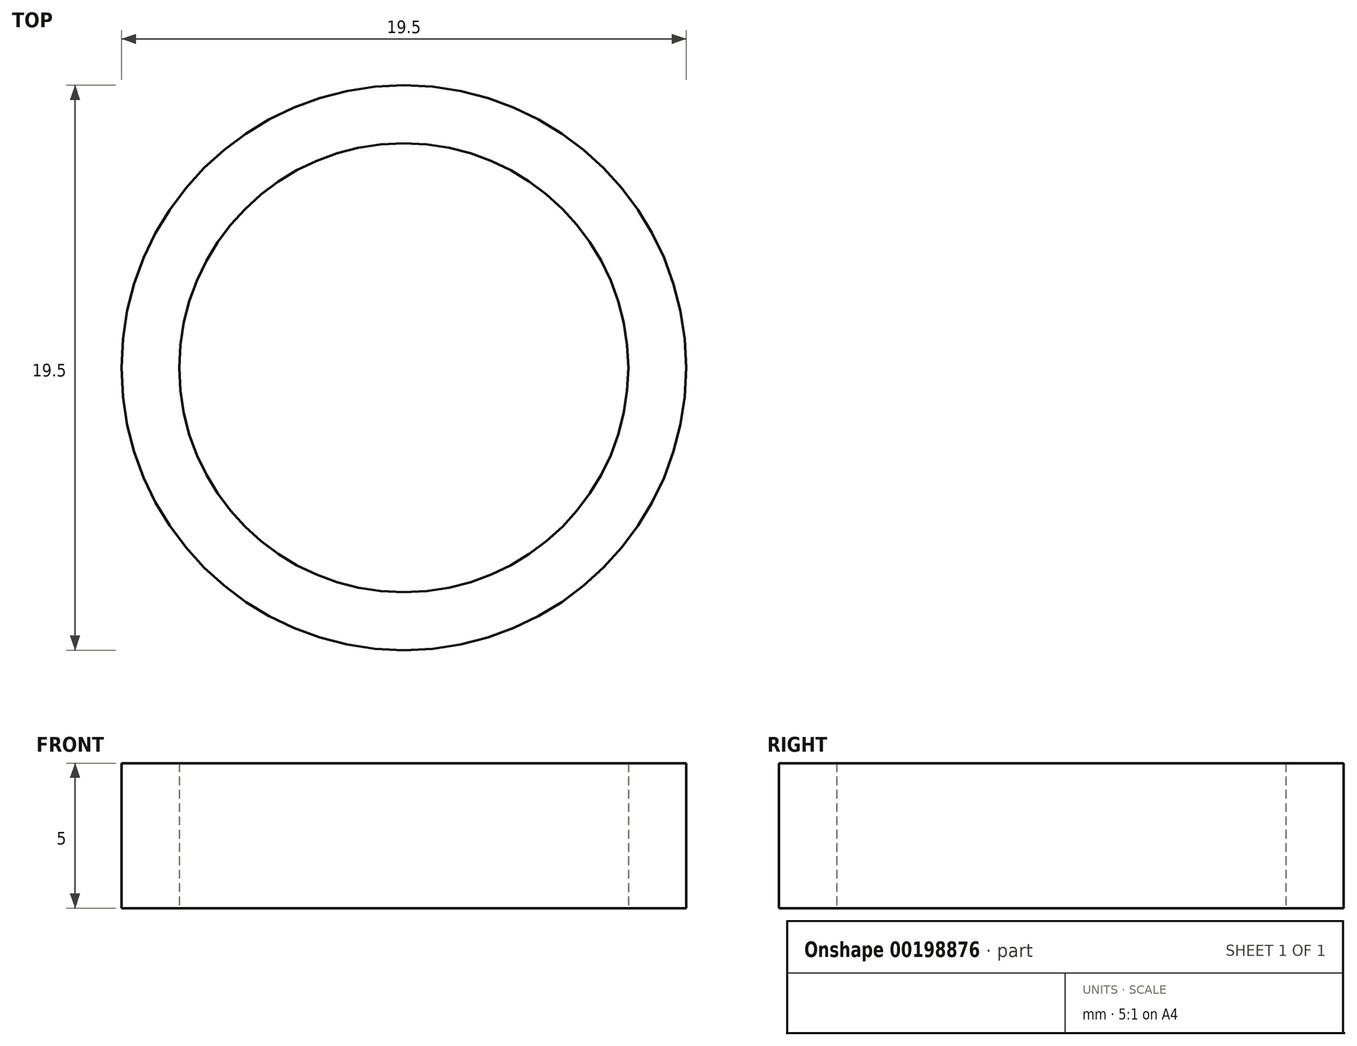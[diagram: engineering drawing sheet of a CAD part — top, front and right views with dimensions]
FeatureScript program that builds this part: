
annotation { "Feature Type Name" : "Feature", "Feature Type Description" : "" }
export const myFeature = defineFeature(function(context is Context, id is Id, definition is map)
    precondition{}
    {
        {
            var Q0;
            Q0=qCreatedBy(makeId("Top.planeOp"),FACE);
            var sketch = newSketch(context, id + "F0", { "sketchPlane" : qUnion([Q0])});
            skCircle(sketch, "E0", {"center": v(0, 0) * mm, "radius": 7.75 * mm});
            skCircle(sketch, "E1", {"center": v(0, 0) * mm, "radius": 9.75 * mm});
            skSolve(sketch);
        }
        {
            var Q0;
            Q0 = qSketchRegion(id + "F0", true);
            extrude(context, id + "F1", {"entities" : qUnion([Q0]), "depth" : 5 * mm});
        }
    });
